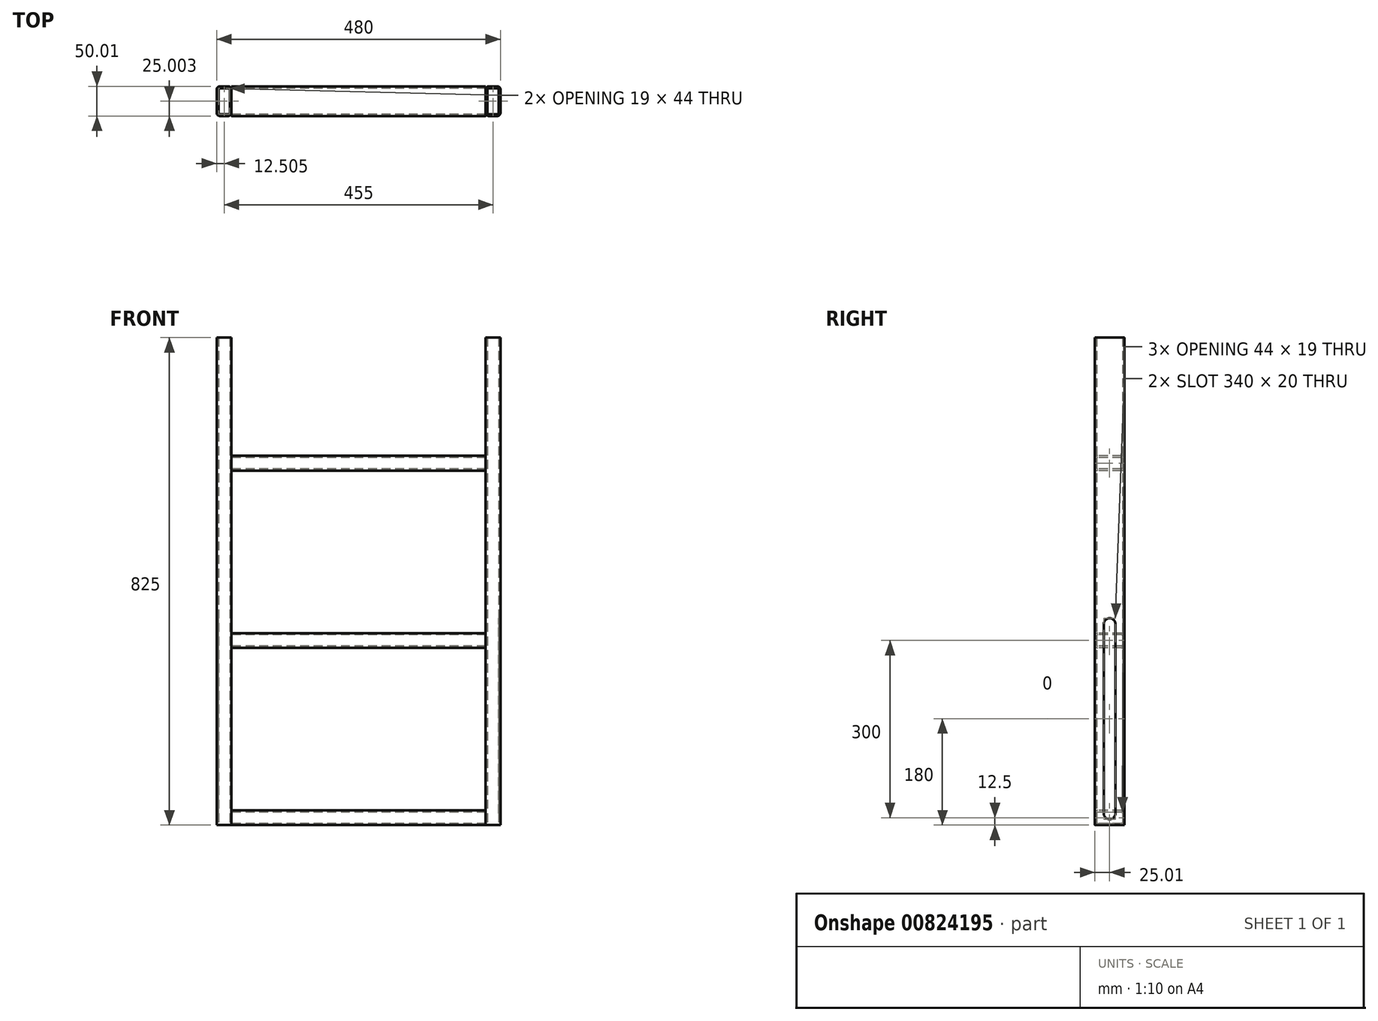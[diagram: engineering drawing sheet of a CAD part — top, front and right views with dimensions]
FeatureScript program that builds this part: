
annotation { "Feature Type Name" : "Feature", "Feature Type Description" : "" }
export const myFeature = defineFeature(function(context is Context, id is Id, definition is map)
    precondition{}
    {
        {
            var Q0;
            Q0=qCreatedBy(makeId("Top.planeOp"),FACE);
            var sketch = newSketch(context, id + "F0", { "sketchPlane" : qUnion([Q0])});
            skLineSegment(sketch, "E0.bottom", {"start": v(12.48, -20) * mm, "end": v(12.48, 20) * mm});
            skLineSegment(sketch, "E0.top", {"start": v(-12.52, -20) * mm, "end": v(-12.52, 20) * mm});
            skLineSegment(sketch, "E0.left", {"start": v(7.48, -25) * mm, "end": v(-7.52, -25) * mm});
            skLineSegment(sketch, "E0.right", {"start": v(7.48, 25) * mm, "end": v(-7.52, 25) * mm});
            skPoint(sketch, "E0.middle", {"position": v(-0.02, 0) * mm});
            skPoint(sketch, "E1.visualSharp", {"position": v(12.48, 25) * mm});
            skArc(sketch, "E1.filletArc", {"start": v(12.48, 20) * mm, "mid": v(11.02, 23.53) * mm, "end": v(7.48, 25) * mm});
            skPoint(sketch, "E2.visualSharp", {"position": v(12.48, -25) * mm});
            skArc(sketch, "E2.filletArc", {"start": v(7.48, -25) * mm, "mid": v(11.02, -23.54) * mm, "end": v(12.48, -20) * mm});
            skPoint(sketch, "E3.visualSharp", {"position": v(-12.52, -25) * mm});
            skArc(sketch, "E3.filletArc", {"start": v(-12.52, -20) * mm, "mid": v(-11.05, -23.54) * mm, "end": v(-7.52, -25) * mm});
            skPoint(sketch, "E4.visualSharp", {"position": v(-12.52, 25) * mm});
            skArc(sketch, "E4.filletArc", {"start": v(-7.52, 25) * mm, "mid": v(-11.05, 23.53) * mm, "end": v(-12.52, 20) * mm});
            skLineSegment(sketch, "E5.0", {"start": v(7.48, 22) * mm, "end": v(-7.52, 22) * mm});
            skLineSegment(sketch, "E5.1", {"start": v(9.48, -20) * mm, "end": v(9.48, 20) * mm});
            skLineSegment(sketch, "E5.2", {"start": v(7.48, -22) * mm, "end": v(-7.52, -22) * mm});
            skLineSegment(sketch, "E5.3", {"start": v(-9.52, -20) * mm, "end": v(-9.52, 20) * mm});
            skPoint(sketch, "E6.visualSharp", {"position": v(9.48, 22) * mm});
            skArc(sketch, "E6.filletArc", {"start": v(9.48, 20) * mm, "mid": v(8.9, 21.4) * mm, "end": v(7.48, 22) * mm});
            skPoint(sketch, "E7.visualSharp", {"position": v(9.48, -22) * mm});
            skArc(sketch, "E7.filletArc", {"start": v(7.48, -22) * mm, "mid": v(8.9, -21.42) * mm, "end": v(9.48, -20) * mm});
            skPoint(sketch, "E8.visualSharp", {"position": v(-9.52, -22) * mm});
            skArc(sketch, "E8.filletArc", {"start": v(-9.52, -20) * mm, "mid": v(-8.93, -21.42) * mm, "end": v(-7.52, -22) * mm});
            skPoint(sketch, "E9.visualSharp", {"position": v(-9.52, 22) * mm});
            skArc(sketch, "E9.filletArc", {"start": v(-7.52, 22) * mm, "mid": v(-8.93, 21.4) * mm, "end": v(-9.52, 20) * mm});
            skSolve(sketch);
        }
        {
            var Q0;
            Q0=makeQuery(id+"F0.imprint","IMPRINT",FACE,{"disambiguationData":[TD([[makeQuery(id+"F0.imprint","IMPRINT",EDGE,{"derivedFrom":sQuery(id+"F0.wireOp",EDGE,"E0.bottom")}),1.0]])]});
            extrude(context, id + "F1", {"entities" : qUnion([Q0]), "depth" : 825 * mm, "offsetDistance" : 25 * mm});
        }
        {
            var Q0;
            Q0=makeQuery(id+"F1.opExtrude","SWEPT_FACE",FACE,{"disambiguationData":[OSD([sQuery(id+"F0.wireOp",EDGE,"E0.top")])]});
            var sketch = newSketch(context, id + "F2", { "sketchPlane" : qUnion([Q0])});
            skLineSegment(sketch, "E10", {"start": v(-20, 20) * mm, "end": v(20, 20) * mm, "construction": true});
            skLineSegment(sketch, "E11", {"start": v(-20, 340) * mm, "end": v(20, 340) * mm, "construction": true});
            skLineSegment(sketch, "E12", {"start": v(0, 370.1) * mm, "end": v(0, 0) * mm, "construction": true});
            skArc(sketch, "E13", {"start": v(10, 340) * mm, "mid": v(0, 350) * mm, "end": v(-10, 340) * mm});
            skArc(sketch, "E14", {"start": v(-10, 20) * mm, "mid": v(0, 10) * mm, "end": v(10, 20) * mm});
            skLineSegment(sketch, "E15", {"start": v(-10, 340) * mm, "end": v(-10, 20) * mm});
            skLineSegment(sketch, "E16", {"start": v(10, 20) * mm, "end": v(10, 340) * mm});
            skSolve(sketch);
        }
        {
            var Q0;
            Q0=makeQuery(id+"F2.imprint","IMPRINT",FACE,{"disambiguationData":[TD([[makeQuery(id+"F2.imprint","IMPRINT",EDGE,{"derivedFrom":sQuery(id+"F2.wireOp",EDGE,"E13")}),1.0]])]});
            extrude(context, id + "F3", {"entities" : qUnion([Q0]), "operationType" : NewBodyOperationType.REMOVE, "oppositeDirection" : true, "depth" : 3 * mm, "offsetDistance" : 25 * mm});
        }
        {
            var Q0;
            Q0=makeQuery(id+"F1.opExtrude","SWEPT_FACE",FACE,{"disambiguationData":[OSD([sQuery(id+"F0.wireOp",EDGE,"E0.bottom")])]});
            var sketch = newSketch(context, id + "F4", { "sketchPlane" : qUnion([Q0])});
            skLineSegment(sketch, "E17", {"start": v(0, 0) * mm, "end": v(0, 825) * mm, "construction": true});
            skLineSegment(sketch, "E18", {"start": v(-20, 612.5) * mm, "end": v(20, 612.5) * mm, "construction": true});
            skLineSegment(sketch, "E19", {"start": v(-20, 312.5) * mm, "end": v(20, 312.5) * mm, "construction": true});
            skLineSegment(sketch, "E20", {"start": v(-20, 12.5) * mm, "end": v(20, 12.5) * mm, "construction": true});
            skLineSegment(sketch, "E21.bottom", {"start": v(20, 625) * mm, "end": v(-20, 625) * mm});
            skLineSegment(sketch, "E21.top", {"start": v(20, 600) * mm, "end": v(-20, 600) * mm});
            skLineSegment(sketch, "E21.left", {"start": v(25, 620) * mm, "end": v(25, 605) * mm});
            skLineSegment(sketch, "E21.right", {"start": v(-25, 620) * mm, "end": v(-25, 605) * mm});
            skPoint(sketch, "E21.middle", {"position": v(0, 612.5) * mm});
            skPoint(sketch, "E22.visualSharp", {"position": v(-25, 625) * mm});
            skArc(sketch, "E22.filletArc", {"start": v(-20, 625) * mm, "mid": v(-23.54, 623.54) * mm, "end": v(-25, 620) * mm});
            skPoint(sketch, "E23.visualSharp", {"position": v(25, 625) * mm});
            skArc(sketch, "E23.filletArc", {"start": v(25, 620) * mm, "mid": v(23.54, 623.54) * mm, "end": v(20, 625) * mm});
            skPoint(sketch, "E24.visualSharp", {"position": v(25, 600) * mm});
            skArc(sketch, "E24.filletArc", {"start": v(20, 600) * mm, "mid": v(23.54, 601.46) * mm, "end": v(25, 605) * mm});
            skPoint(sketch, "E25.visualSharp", {"position": v(-25, 600) * mm});
            skArc(sketch, "E25.filletArc", {"start": v(-25, 605) * mm, "mid": v(-23.54, 601.46) * mm, "end": v(-20, 600) * mm});
            skLineSegment(sketch, "E26.0", {"start": v(-22, 620) * mm, "end": v(-22, 605) * mm});
            skLineSegment(sketch, "E26.1", {"start": v(20, 622) * mm, "end": v(-20, 622) * mm});
            skLineSegment(sketch, "E26.2", {"start": v(22, 620) * mm, "end": v(22, 605) * mm});
            skLineSegment(sketch, "E26.3", {"start": v(20, 603) * mm, "end": v(-20, 603) * mm});
            skPoint(sketch, "E27.visualSharp", {"position": v(-22, 622) * mm});
            skArc(sketch, "E27.filletArc", {"start": v(-20, 622) * mm, "mid": v(-21.41, 621.41) * mm, "end": v(-22, 620) * mm});
            skPoint(sketch, "E28.visualSharp", {"position": v(22, 622) * mm});
            skArc(sketch, "E28.filletArc", {"start": v(22, 620) * mm, "mid": v(21.41, 621.41) * mm, "end": v(20, 622) * mm});
            skPoint(sketch, "E29.visualSharp", {"position": v(22, 603) * mm});
            skArc(sketch, "E29.filletArc", {"start": v(20, 603) * mm, "mid": v(21.41, 603.59) * mm, "end": v(22, 605) * mm});
            skPoint(sketch, "E30.visualSharp", {"position": v(-22, 603) * mm});
            skArc(sketch, "E30.filletArc", {"start": v(-22, 605) * mm, "mid": v(-21.41, 603.59) * mm, "end": v(-20, 603) * mm});
            skLineSegment(sketch, "E31.bottom", {"start": v(20, 325) * mm, "end": v(-20, 325) * mm});
            skLineSegment(sketch, "E31.top", {"start": v(20, 300) * mm, "end": v(-20, 300) * mm});
            skLineSegment(sketch, "E31.left", {"start": v(25, 320) * mm, "end": v(25, 305) * mm});
            skLineSegment(sketch, "E31.right", {"start": v(-25, 320) * mm, "end": v(-25, 305) * mm});
            skPoint(sketch, "E31.middle", {"position": v(0, 312.5) * mm});
            skPoint(sketch, "E32.visualSharp", {"position": v(-25, 325) * mm});
            skArc(sketch, "E32.filletArc", {"start": v(-20, 325) * mm, "mid": v(-23.54, 323.54) * mm, "end": v(-25, 320) * mm});
            skPoint(sketch, "E33.visualSharp", {"position": v(25, 325) * mm});
            skArc(sketch, "E33.filletArc", {"start": v(25, 320) * mm, "mid": v(23.54, 323.54) * mm, "end": v(20, 325) * mm});
            skPoint(sketch, "E34.visualSharp", {"position": v(25, 300) * mm});
            skArc(sketch, "E34.filletArc", {"start": v(20, 300) * mm, "mid": v(23.54, 301.46) * mm, "end": v(25, 305) * mm});
            skPoint(sketch, "E35.visualSharp", {"position": v(-25, 300) * mm});
            skArc(sketch, "E35.filletArc", {"start": v(-25, 305) * mm, "mid": v(-23.54, 301.46) * mm, "end": v(-20, 300) * mm});
            skLineSegment(sketch, "E36.0", {"start": v(-22, 320) * mm, "end": v(-22, 305) * mm});
            skLineSegment(sketch, "E36.1", {"start": v(20, 322) * mm, "end": v(-20, 322) * mm});
            skLineSegment(sketch, "E36.2", {"start": v(22, 320) * mm, "end": v(22, 305) * mm});
            skLineSegment(sketch, "E36.3", {"start": v(20, 303) * mm, "end": v(-20, 303) * mm});
            skPoint(sketch, "E37.visualSharp", {"position": v(-22, 322) * mm});
            skArc(sketch, "E37.filletArc", {"start": v(-20, 322) * mm, "mid": v(-21.41, 321.41) * mm, "end": v(-22, 320) * mm});
            skPoint(sketch, "E38.visualSharp", {"position": v(22, 322) * mm});
            skArc(sketch, "E38.filletArc", {"start": v(22, 320) * mm, "mid": v(21.41, 321.41) * mm, "end": v(20, 322) * mm});
            skPoint(sketch, "E39.visualSharp", {"position": v(22, 303) * mm});
            skArc(sketch, "E39.filletArc", {"start": v(20, 303) * mm, "mid": v(21.41, 303.59) * mm, "end": v(22, 305) * mm});
            skPoint(sketch, "E40.visualSharp", {"position": v(-22, 303) * mm});
            skArc(sketch, "E40.filletArc", {"start": v(-22, 305) * mm, "mid": v(-21.41, 303.59) * mm, "end": v(-20, 303) * mm});
            skLineSegment(sketch, "E41.bottom", {"start": v(20, 25) * mm, "end": v(-20, 25) * mm});
            skLineSegment(sketch, "E41.top", {"start": v(20, 0) * mm, "end": v(-20, 0) * mm});
            skLineSegment(sketch, "E41.left", {"start": v(25, 20) * mm, "end": v(25, 5) * mm});
            skLineSegment(sketch, "E41.right", {"start": v(-25, 20) * mm, "end": v(-25, 5) * mm});
            skPoint(sketch, "E41.middle", {"position": v(0, 12.5) * mm});
            skPoint(sketch, "E42.visualSharp", {"position": v(-25, 25) * mm});
            skArc(sketch, "E42.filletArc", {"start": v(-20, 25) * mm, "mid": v(-23.54, 23.54) * mm, "end": v(-25, 20) * mm});
            skPoint(sketch, "E43.visualSharp", {"position": v(25, 25) * mm});
            skArc(sketch, "E43.filletArc", {"start": v(25, 20) * mm, "mid": v(23.54, 23.54) * mm, "end": v(20, 25) * mm});
            skPoint(sketch, "E44.visualSharp", {"position": v(25, 0) * mm});
            skArc(sketch, "E44.filletArc", {"start": v(20, 0) * mm, "mid": v(23.54, 1.46) * mm, "end": v(25, 5) * mm});
            skPoint(sketch, "E45.visualSharp", {"position": v(-25, 0) * mm});
            skArc(sketch, "E45.filletArc", {"start": v(-25, 5) * mm, "mid": v(-23.54, 1.46) * mm, "end": v(-20, 0) * mm});
            skLineSegment(sketch, "E46.0", {"start": v(-22, 20) * mm, "end": v(-22, 5) * mm});
            skLineSegment(sketch, "E46.1", {"start": v(20, 22) * mm, "end": v(-20, 22) * mm});
            skLineSegment(sketch, "E46.2", {"start": v(22, 20) * mm, "end": v(22, 5) * mm});
            skLineSegment(sketch, "E46.3", {"start": v(20, 3) * mm, "end": v(-20, 3) * mm});
            skPoint(sketch, "E47.visualSharp", {"position": v(-22, 22) * mm});
            skArc(sketch, "E47.filletArc", {"start": v(-20, 22) * mm, "mid": v(-21.41, 21.41) * mm, "end": v(-22, 20) * mm});
            skPoint(sketch, "E48.visualSharp", {"position": v(22, 22) * mm});
            skArc(sketch, "E48.filletArc", {"start": v(22, 20) * mm, "mid": v(21.41, 21.41) * mm, "end": v(20, 22) * mm});
            skPoint(sketch, "E49.visualSharp", {"position": v(22, 3) * mm});
            skArc(sketch, "E49.filletArc", {"start": v(20, 3) * mm, "mid": v(21.41, 3.59) * mm, "end": v(22, 5) * mm});
            skPoint(sketch, "E50.visualSharp", {"position": v(-22, 3) * mm});
            skArc(sketch, "E50.filletArc", {"start": v(-22, 5) * mm, "mid": v(-21.41, 3.59) * mm, "end": v(-20, 3) * mm});
            skSolve(sketch);
        }
        {
            var Q0;
            {var subQ8=sQuery(id+"F4.wireOp",EDGE,"E42.filletArc");var subQ10=sQuery(id+"F4.wireOp",EDGE,"E41.bottom");var subQ11=makeQuery(id+"F4.imprint","INTERSECT",VERTEX,{"derivedFrom":[subQ10,subQ8]});Q0=makeQuery(id+"F4.imprint","IMPRINT",FACE,{"disambiguationData":[TD([[makeQuery(id+"F4.imprint","IMPRINT",EDGE,{"disambiguationData":[TD([[subQ11,1.0]])],"derivedFrom":subQ10}),1.0]])]});}
            var Q1;
            {var subQ0=sQuery(id+"F4.wireOp",EDGE,"E50.filletArc");var subQ1=sQuery(id+"F4.wireOp",EDGE,"E46.3");var subQ2=makeQuery(id+"F4.imprint","INTERSECT",VERTEX,{"derivedFrom":[subQ1,subQ0]});Q1=makeQuery(id+"F4.imprint","IMPRINT",FACE,{"disambiguationData":[TD([[makeQuery(id+"F4.imprint","IMPRINT",EDGE,{"disambiguationData":[TD([[subQ2,1.0]])],"derivedFrom":subQ1}),1.0]])]});}
            var Q2;
            {var subQ2=sQuery(id+"F4.wireOp",EDGE,"E41.right");Q2=makeQuery(id+"F4.imprint","IMPRINT",FACE,{"disambiguationData":[TD([[makeQuery(id+"F4.imprint","IMPRINT",EDGE,{"derivedFrom":subQ2}),1.0]])]});}
            var Q3;
            Q3=makeQuery(id+"F4.imprint","IMPRINT",FACE,{"disambiguationData":[TD([[makeQuery(id+"F4.imprint","IMPRINT",EDGE,{"derivedFrom":sQuery(id+"F4.wireOp",EDGE,"E41.left")}),-1.0]])]});
            extrude(context, id + "F5", {"entities" : qUnion([Q0, Q1, Q2, Q3]), "depth" : 430 * mm, "offsetDistance" : 25 * mm});
        }
        {
            var Q0;
            {var subQ8=sQuery(id+"F4.wireOp",EDGE,"E32.filletArc");var subQ10=sQuery(id+"F4.wireOp",EDGE,"E31.bottom");var subQ11=makeQuery(id+"F4.imprint","INTERSECT",VERTEX,{"derivedFrom":[subQ10,subQ8]});Q0=makeQuery(id+"F4.imprint","IMPRINT",FACE,{"disambiguationData":[TD([[makeQuery(id+"F4.imprint","IMPRINT",EDGE,{"disambiguationData":[TD([[subQ11,1.0]])],"derivedFrom":subQ10}),1.0]])]});}
            var Q1;
            Q1=makeQuery(id+"F4.imprint","IMPRINT",FACE,{"disambiguationData":[TD([[makeQuery(id+"F4.imprint","IMPRINT",EDGE,{"derivedFrom":sQuery(id+"F4.wireOp",EDGE,"E31.left")}),-1.0]])]});
            var Q2;
            {var subQ6=sQuery(id+"F4.wireOp",EDGE,"E35.filletArc");var subQ7=sQuery(id+"F4.wireOp",EDGE,"E31.top");var subQ8=makeQuery(id+"F4.imprint","INTERSECT",VERTEX,{"derivedFrom":[subQ7,subQ6]});Q2=makeQuery(id+"F4.imprint","IMPRINT",FACE,{"disambiguationData":[TD([[makeQuery(id+"F4.imprint","IMPRINT",EDGE,{"disambiguationData":[TD([[subQ8,1.0]])],"derivedFrom":subQ7}),-1.0]])]});}
            var Q3;
            {var subQ2=sQuery(id+"F4.wireOp",EDGE,"E31.right");Q3=makeQuery(id+"F4.imprint","IMPRINT",FACE,{"disambiguationData":[TD([[makeQuery(id+"F4.imprint","IMPRINT",EDGE,{"derivedFrom":subQ2}),1.0]])]});}
            extrude(context, id + "F6", {"entities" : qUnion([Q0, Q1, Q2, Q3]), "depth" : 430 * mm, "offsetDistance" : 25 * mm});
        }
        {
            var Q0;
            {var subQ2=sQuery(id+"F4.wireOp",EDGE,"E21.right");Q0=makeQuery(id+"F4.imprint","IMPRINT",FACE,{"disambiguationData":[TD([[makeQuery(id+"F4.imprint","IMPRINT",EDGE,{"derivedFrom":subQ2}),1.0]])]});}
            var Q1;
            {var subQ6=sQuery(id+"F4.wireOp",EDGE,"E25.filletArc");var subQ7=sQuery(id+"F4.wireOp",EDGE,"E21.top");var subQ8=makeQuery(id+"F4.imprint","INTERSECT",VERTEX,{"derivedFrom":[subQ7,subQ6]});Q1=makeQuery(id+"F4.imprint","IMPRINT",FACE,{"disambiguationData":[TD([[makeQuery(id+"F4.imprint","IMPRINT",EDGE,{"disambiguationData":[TD([[subQ8,1.0]])],"derivedFrom":subQ7}),-1.0]])]});}
            var Q2;
            Q2=makeQuery(id+"F4.imprint","IMPRINT",FACE,{"disambiguationData":[TD([[makeQuery(id+"F4.imprint","IMPRINT",EDGE,{"derivedFrom":sQuery(id+"F4.wireOp",EDGE,"E21.left")}),-1.0]])]});
            var Q3;
            {var subQ8=sQuery(id+"F4.wireOp",EDGE,"E22.filletArc");var subQ10=sQuery(id+"F4.wireOp",EDGE,"E21.bottom");var subQ11=makeQuery(id+"F4.imprint","INTERSECT",VERTEX,{"derivedFrom":[subQ10,subQ8]});Q3=makeQuery(id+"F4.imprint","IMPRINT",FACE,{"disambiguationData":[TD([[makeQuery(id+"F4.imprint","IMPRINT",EDGE,{"disambiguationData":[TD([[subQ11,1.0]])],"derivedFrom":subQ10}),1.0]])]});}
            extrude(context, id + "F7", {"entities" : qUnion([Q0, Q1, Q2, Q3]), "depth" : 430 * mm, "offsetDistance" : 25 * mm});
        }
        {
            var Q0;
            Q0=makeQuery(id+"F1.opExtrude","SWEPT_BODY",BODY,{"disambiguationData":[OSD([sQuery(id+"F0.wireOp",EDGE,"E0.bottom"),sQuery(id+"F0.wireOp",EDGE,"E0.top"),sQuery(id+"F0.wireOp",EDGE,"E0.left"),sQuery(id+"F0.wireOp",EDGE,"E0.right"),sQuery(id+"F0.wireOp",EDGE,"E1.filletArc"),sQuery(id+"F0.wireOp",EDGE,"E2.filletArc"),sQuery(id+"F0.wireOp",EDGE,"E3.filletArc"),sQuery(id+"F0.wireOp",EDGE,"E4.filletArc"),sQuery(id+"F0.wireOp",EDGE,"E5.0"),sQuery(id+"F0.wireOp",EDGE,"E5.1"),sQuery(id+"F0.wireOp",EDGE,"E5.2"),sQuery(id+"F0.wireOp",EDGE,"E5.3"),sQuery(id+"F0.wireOp",EDGE,"E6.filletArc"),sQuery(id+"F0.wireOp",EDGE,"E7.filletArc"),sQuery(id+"F0.wireOp",EDGE,"E8.filletArc"),sQuery(id+"F0.wireOp",EDGE,"E9.filletArc")])]});
            var Q1;
            Q1=makeQuery(id+"F1.opExtrude","SWEPT_FACE",FACE,{"disambiguationData":[OSD([sQuery(id+"F0.wireOp",EDGE,"E0.bottom")])]});
            mirror(context, id + "F8", {"entities" : qUnion([Q0]), "mirrorPlane" : qUnion([Q1])});
        }
        {
            var Q0;
            Q0=makeQuery(id+"F8.opPattern","COPY",BODY,{"derivedFrom":makeQuery(id+"F1.opExtrude","SWEPT_BODY",BODY,{"disambiguationData":[OSD([sQuery(id+"F0.wireOp",EDGE,"E0.bottom"),sQuery(id+"F0.wireOp",EDGE,"E0.top"),sQuery(id+"F0.wireOp",EDGE,"E0.left"),sQuery(id+"F0.wireOp",EDGE,"E0.right"),sQuery(id+"F0.wireOp",EDGE,"E1.filletArc"),sQuery(id+"F0.wireOp",EDGE,"E2.filletArc"),sQuery(id+"F0.wireOp",EDGE,"E3.filletArc"),sQuery(id+"F0.wireOp",EDGE,"E4.filletArc"),sQuery(id+"F0.wireOp",EDGE,"E5.0"),sQuery(id+"F0.wireOp",EDGE,"E5.1"),sQuery(id+"F0.wireOp",EDGE,"E5.2"),sQuery(id+"F0.wireOp",EDGE,"E5.3"),sQuery(id+"F0.wireOp",EDGE,"E6.filletArc"),sQuery(id+"F0.wireOp",EDGE,"E7.filletArc"),sQuery(id+"F0.wireOp",EDGE,"E8.filletArc"),sQuery(id+"F0.wireOp",EDGE,"E9.filletArc")])]}),"instanceName":"1"});
            transform(context, id + "F9", {"entities" : qUnion([Q0]), "transformType" : TransformType.TRANSLATION_3D, "dx" : 430 * mm, "dy" : 0 * mm, "dz" : 0 * mm, "makeCopy" : false});
        }
    });
